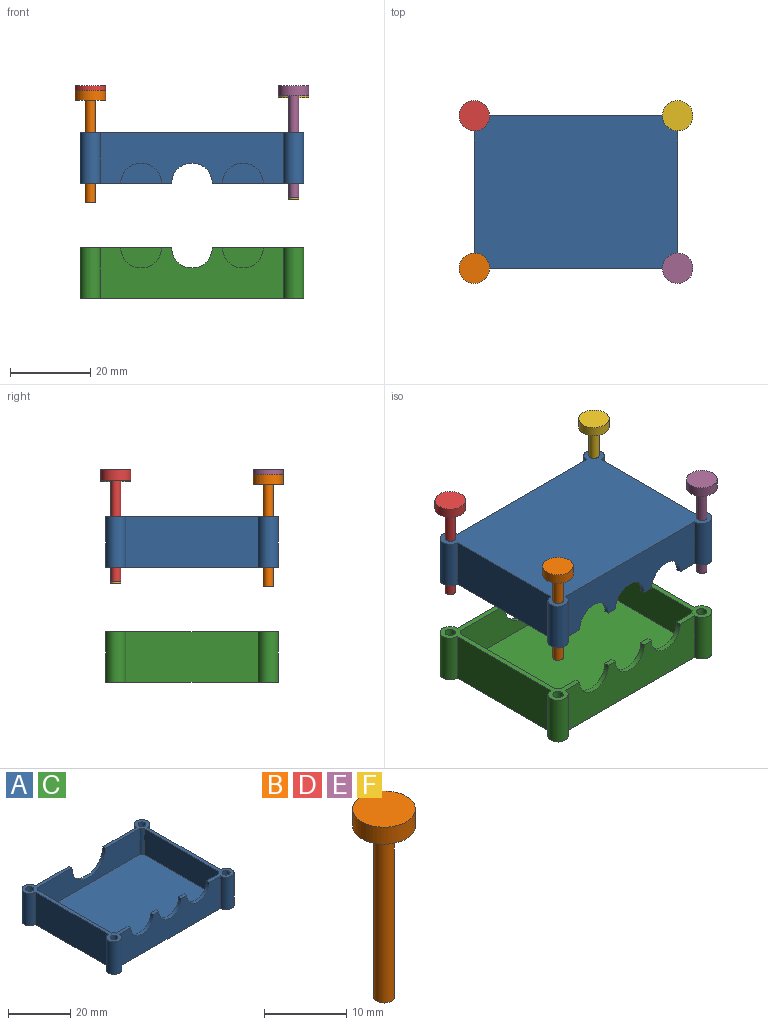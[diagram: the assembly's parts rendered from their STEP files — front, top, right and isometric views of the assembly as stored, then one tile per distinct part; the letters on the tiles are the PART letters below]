
ASSEMBLY  parts=6 mates=9
PART A: 30 faces, bbox 55.9x43.2x12.7 mm
  f0: plane 43.18x20.32mm, normal (0,0,1), area 98.7mm2, adj f3,f6,f7,f9,f11,f12,f16,f17
  f1: plane 43.18x20.32mm, normal (0,0,1), area 98.7mm2, adj f3,f5,f7,f9,f10,f11,f14,f15
  f2: plane 2.54x1.27mm, normal (0,0,1), area 3.2mm2, adj f3,f11,f27,f28
  f3: plane 45.72x12.7mm, normal (0,-1,0), area 459mm2, adj f0,f1,f2,f4,f8,f15,f17,f26
  f4: plane 2.54x1.27mm, normal (0,0,1), area 3.2mm2, adj f3,f11,f26,f27
  f5: plane 33.02x12.7mm, normal (-1,0,0), area 419.4mm2, adj f1,f8,f15,f21
  f6: plane 33.02x12.7mm, normal (1,0,0), area 419.4mm2, adj f0,f8,f17,f19
  f7: plane 45.72x12.7mm, normal (0,1,0), area 489.4mm2, adj f0,f1,f8,f19,f21,f29
  f8: plane 55.88x43.18mm, normal (0,0,-1), area 1976mm2, adj f3,f5,f6,f7,f15,f17,f19,f21
  f9: plane 46.4x10.16mm, normal (0,-1,0), area 380.2mm2, adj f0,f1,f13,f18,f20,f29
  f10: plane 33.7x10.16mm, normal (1,0,0), area 342.4mm2, adj f1,f13,f14,f20
  f11: plane 46.4x10.16mm, normal (0,1,0), area 349.8mm2, adj f0,f1,f2,f4,f13,f14,f16,f26
  f12: plane 33.7x10.16mm, normal (-1,0,0), area 342.4mm2, adj f0,f13,f16,f18
  f13: plane 48.26x35.56mm, normal (0,0,1), area 1714.1mm2, adj f9,f10,f11,f12,f14,f16,f18,f20
  f14: cylinder r=2.54mm len=10.16mm, axis (0,0,-1), area 13.5mm2, adj f1,f10,f11,f13
  f15: cylinder r=2.54mm len=12.7mm, axis (0,0,-1), area 152mm2, adj f1,f3,f5,f8
  f16: cylinder r=2.54mm len=10.16mm, axis (0,0,-1), area 13.5mm2, adj f0,f11,f12,f13
  f17: cylinder r=2.54mm len=12.7mm, axis (0,0,-1), area 152mm2, adj f0,f3,f6,f8
  f18: cylinder r=2.54mm len=10.16mm, axis (0,0,-1), area 13.5mm2, adj f0,f9,f12,f13
  f19: cylinder r=2.54mm len=12.7mm, axis (0,0,-1), area 152mm2, adj f0,f6,f7,f8
  f20: cylinder r=2.54mm len=10.16mm, axis (0,0,-1), area 13.5mm2, adj f1,f9,f10,f13
  f21: cylinder r=2.54mm len=12.7mm, axis (0,0,-1), area 152mm2, adj f1,f5,f7,f8
  f22: cylinder r=1.27mm len=12.7mm, axis (0,0,1), area 101.3mm2, adj f1,f8
  f23: cylinder r=1.27mm len=12.7mm, axis (0,0,1), area 101.3mm2, adj f1,f8
  f24: cylinder r=1.27mm len=12.7mm, axis (0,0,1), area 101.3mm2, adj f0,f8
  f25: cylinder r=1.27mm len=12.7mm, axis (0,0,1), area 101.3mm2, adj f0,f8
  f26: cylinder r=5.08mm len=10.16mm, axis (0,-1,0), area 20.3mm2, adj f0,f3,f4,f11
  f27: cylinder r=5.08mm len=10.16mm, axis (0,-1,0), area 20.3mm2, adj f2,f3,f4,f11
  f28: cylinder r=5.08mm len=10.16mm, axis (0,-1,0), area 20.3mm2, adj f1,f2,f3,f11
  f29: cylinder r=7.62mm len=15.24mm, axis (0,1,0), area 30.4mm2, adj f0,f1,f7,f9
PART B: 5 faces, bbox 7.6x7.6x27.9 mm
  f0: cylinder r=1.27mm len=25.4mm, axis (0,0,-1), area 202.7mm2, adj f1,f4
  f1: plane 2.54x2.54mm, normal (0,0,-1), area 5.1mm2, adj f0
  f2: cylinder r=3.81mm len=7.62mm, axis (0,0,-1), area 60.8mm2, adj f3,f4
  f3: plane 7.62x7.62mm, normal (0,0,1), area 45.6mm2, adj f2
  f4: plane 7.62x7.62mm, normal (0,0,-1), area 40.5mm2, adj f0,f2
PART C: same geometry as A
PART D: same geometry as B
PART E: same geometry as B
PART F: same geometry as B
PLACE A rot(axis=(0,1,0),180deg) t=(25.4,-19.05,41.45)mm
PLACE B t=(-25.4,-19.05,24.08)mm
PLACE C t=(-25.4,-19.05,0)mm
PLACE D t=(-25.4,19.05,25.15)mm
PLACE E t=(25.4,-19.05,25.27)mm
PLACE F t=(25.4,19.05,24.7)mm
MATE slider B.f0 <-> C.f14  axis (0,0,-1) through (-25.4,-19.05,24.08)mm
MATE slider B.f0 <-> A.f24  axis (0,0,-1) through (-25.4,-19.05,36.78)mm
MATE slider D.f0 <-> C.f20  axis (0,0,-1) through (-25.4,19.05,37.85)mm
MATE slider F.f0 <-> A.f20  axis (0,0,-1) through (25.4,19.05,37.4)mm
MATE slider E.f0 <-> A.f14  axis (0,0,-1) through (25.4,-19.05,37.97)mm
MATE slider F.f0 <-> C.f18  axis (0,0,-1) through (25.4,19.05,37.4)mm
MATE slider D.f0 <-> A.f18  axis (0,0,-1) through (-25.4,19.05,37.85)mm
MATE slider E.f0 <-> C.f24  axis (0,0,-1) through (25.4,-19.05,37.97)mm
MATE parallel C.f14 <-> A.f16  axis (0,0,1) through (-25.4,-19.05,12.7)mm
